# Revit family: TEMID_Терминал биометрический с распознаванием лиц ладоней и карт ProFaceХ_WIFI
name_source: partatom
category: Охранная сигнализация
units: mm (PartAtom-declared; Revit-internal decimal feet)

## family parameters
Всегда вертикально = Нет
На основе рабочей плоскости = Нет
Общий = Да
При загрузке вырезать с полостями = Нет
Размер круглого соединителя = Использовать диаметр
Сохранять ориентацию аннотаций = Нет
Тип детали = Нормальный
Точка расчета площади = Да

## types (2) — shared parameters
=Габариты= = =Габариты=
ADSK_Единица измерения = шт.
ADSK_Завод-изготовитель = TEMID
ADSK_Количество = 1
ADSK_Обозначение = RD
ADSK_Раздел спецификации = 3. Периферийное оборудование
ADSK_Размер_Высота = 273 мм
ADSK_Размер_Глубина = 26 мм
ADSK_Размер_Ширина = 143 мм
URL = https://temid-global.ru
Зона обслуживания_Отступ от прибора = 50 мм
Коронштейн крепления = Да
Материал = Серый
zero-valued in all types: Отметка по умолчанию

## per-type parameters (varying)
| type | ADSK_Марка | ADSK_Наименование | ADSK_Тип |
| ProFaceX-P | ProFaceX[P] | Биометрический терминал распознавания лиц, рисунка ладоней, считыватель, дисплей 8" TFT, память: лиц 30000, ладонь 5 тыс,карт 50 000, событий 1 млн. TCP/IP, 2хUSB,RS232, RS485, уличный, IP68, -30  +60 град. | ProFaceX[P] |
| ProFaceX-P-WIFI | ProFaceX[P] [WIFI] | Биометрический терминал распознавания лиц, рисунка ладоней, считыватель, дисплей 8" TFT, память: лиц 30000, ладонь 5 тыс,карт 50 000, событий 1 млн. TCP/IP, 2хUSB,RS232, RS485, уличный, IP68, -30  +60 град., с функцией WIFI | ProFaceX[P] [WIFI] |
